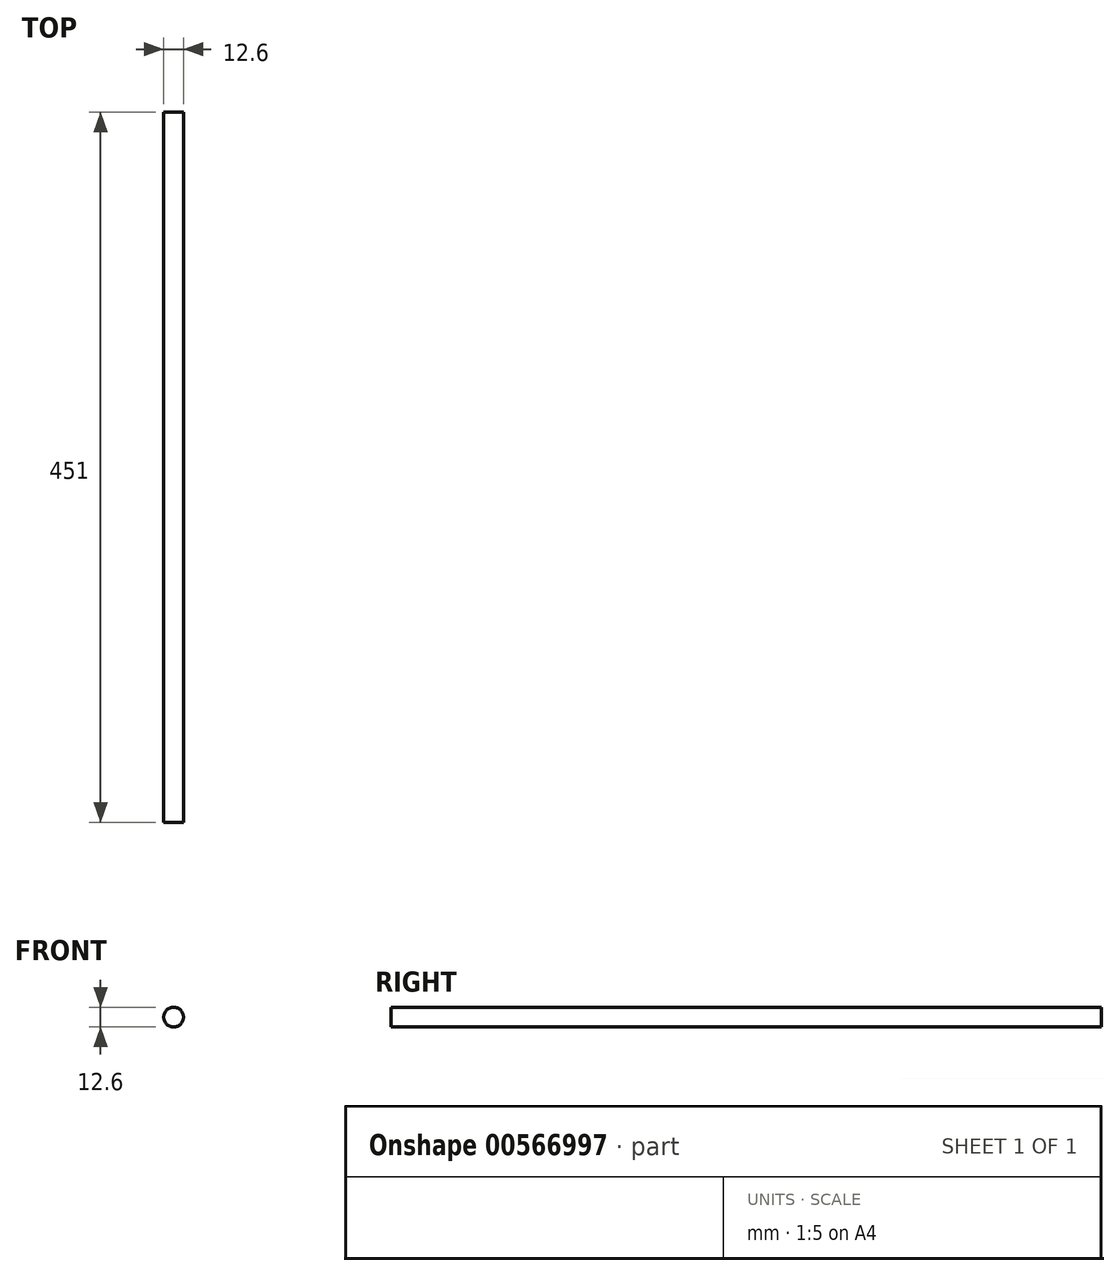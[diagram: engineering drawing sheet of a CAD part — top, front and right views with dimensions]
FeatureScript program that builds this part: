
annotation { "Feature Type Name" : "Feature", "Feature Type Description" : "" }
export const myFeature = defineFeature(function(context is Context, id is Id, definition is map)
    precondition{}
    {
        {
            var Q0;
            Q0=qCreatedBy(makeId("Front.planeOp"),FACE);
            var sketch = newSketch(context, id + "F0", { "sketchPlane" : qUnion([Q0])});
            skCircle(sketch, "E0", {"center": v(0, 0) * mm, "radius": 6.3 * mm});
            skSolve(sketch);
        }
        {
            var Q0;
            Q0 = qSketchRegion(id + "F0", true);
            extrude(context, id + "F1", {"entities" : qUnion([Q0]), "depth" : 451 * mm, "offsetDistance" : 25 * mm});
        }
    });
